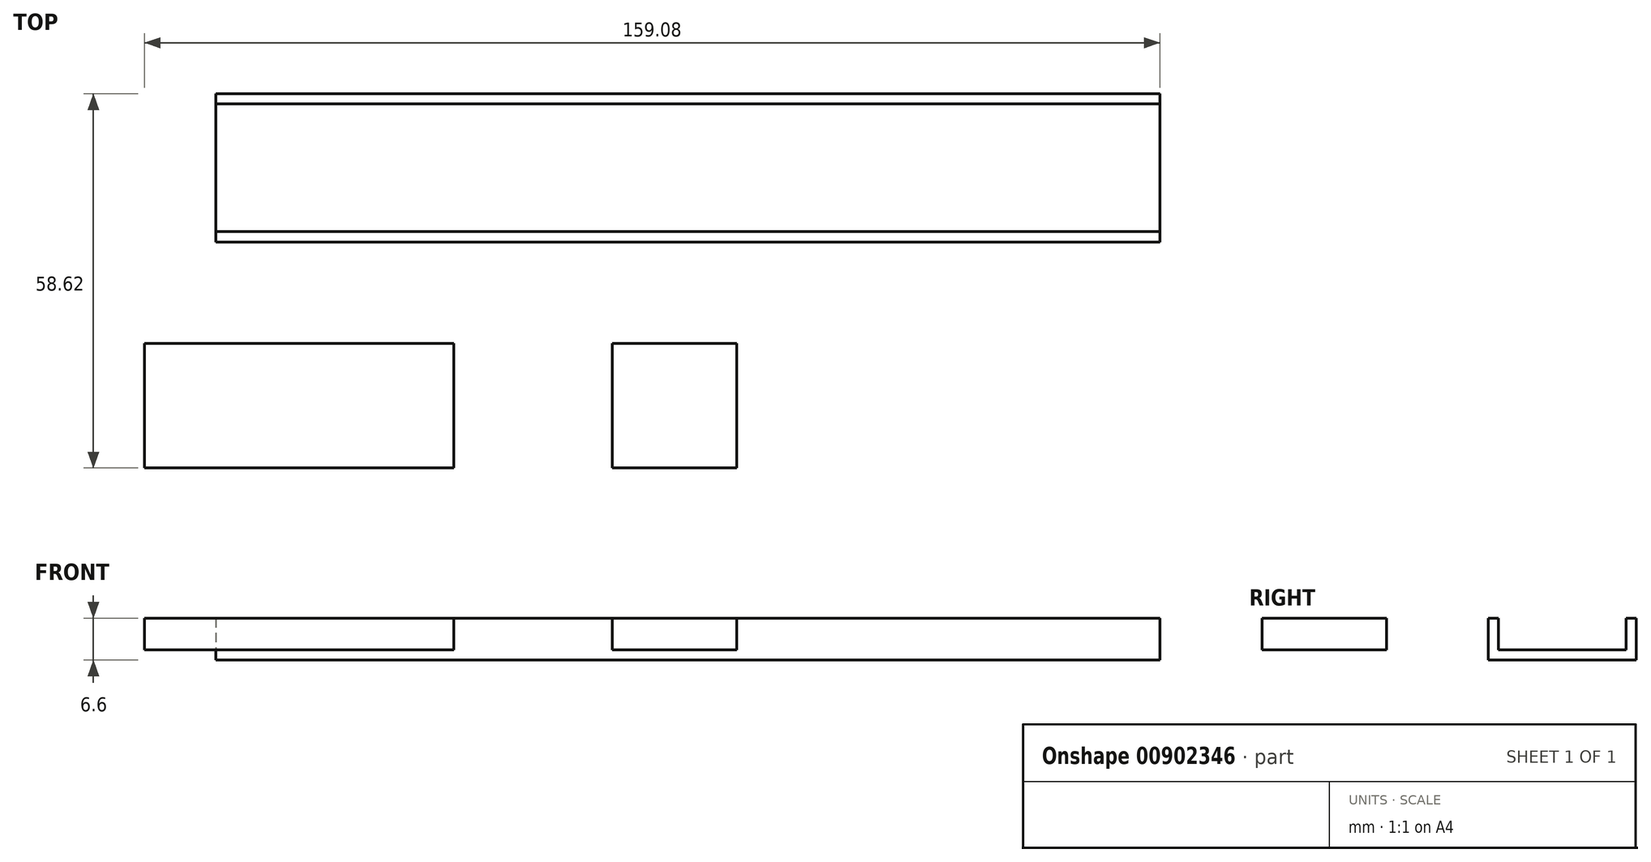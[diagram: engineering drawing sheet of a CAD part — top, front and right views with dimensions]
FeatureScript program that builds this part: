
annotation { "Feature Type Name" : "Feature", "Feature Type Description" : "" }
export const myFeature = defineFeature(function(context is Context, id is Id, definition is map)
    precondition{}
    {
        {
            var Q0;
            Q0=qCreatedBy(makeId("Top.planeOp"),FACE);
            var sketch = newSketch(context, id + "F0", { "sketchPlane" : qUnion([Q0])});
            skLineSegment(sketch, "E0.bottom", {"start": v(0, 0) * mm, "end": v(19.5, 0) * mm});
            skLineSegment(sketch, "E0.top", {"start": v(0, -19.5) * mm, "end": v(19.5, -19.5) * mm});
            skLineSegment(sketch, "E0.left", {"start": v(0, 0) * mm, "end": v(0, -19.5) * mm});
            skLineSegment(sketch, "E0.right", {"start": v(19.5, 0) * mm, "end": v(19.5, -19.5) * mm});
            skLineSegment(sketch, "E1.bottom", {"start": v(-24.79, 0) * mm, "end": v(-73.26, 0) * mm});
            skLineSegment(sketch, "E1.top", {"start": v(-24.79, -19.5) * mm, "end": v(-73.26, -19.5) * mm});
            skLineSegment(sketch, "E1.left", {"start": v(-24.79, 0) * mm, "end": v(-24.79, -19.5) * mm});
            skLineSegment(sketch, "E1.right", {"start": v(-73.26, 0) * mm, "end": v(-73.26, -19.5) * mm});
            skSolve(sketch);
        }
        {
            var Q0;
            Q0 = qSketchRegion(id + "F0", true);
            extrude(context, id + "F1", {"entities" : qUnion([Q0]), "depth" : 5 * mm, "offsetDistance" : 25 * mm});
        }
        {
            var Q0;
            Q0=qCreatedBy(makeId("Top.planeOp"),FACE);
            var sketch = newSketch(context, id + "F2", { "sketchPlane" : qUnion([Q0])});
            skLineSegment(sketch, "E2.bottom", {"start": v(-62.1, 37.52) * mm, "end": v(85.82, 37.52) * mm});
            skLineSegment(sketch, "E2.top", {"start": v(-62.1, 17.52) * mm, "end": v(85.82, 17.52) * mm});
            skLineSegment(sketch, "E2.left", {"start": v(-62.1, 37.52) * mm, "end": v(-62.1, 17.52) * mm});
            skLineSegment(sketch, "E2.right", {"start": v(85.82, 37.52) * mm, "end": v(85.82, 17.52) * mm});
            skSolve(sketch);
        }
        {
            var Q0;
            Q0 = qSketchRegion(id + "F2", true);
            extrude(context, id + "F3", {"entities" : qUnion([Q0]), "depth" : 5 * mm, "offsetDistance" : 25 * mm});
        }
        {
            var Q0;
            Q0=makeQuery(id+"F3.opExtrude","CAP_FACE",FACE,{"disambiguationData":[OSD([sQuery(id+"F2.wireOp",EDGE,"E2.bottom"),sQuery(id+"F2.wireOp",EDGE,"E2.top"),sQuery(id+"F2.wireOp",EDGE,"E2.left"),sQuery(id+"F2.wireOp",EDGE,"E2.right")])],"isStart":false});
            var Q1;
            Q1=makeQuery(id+"F3.opExtrude","SWEPT_FACE",FACE,{"disambiguationData":[OSD([sQuery(id+"F2.wireOp",EDGE,"E2.left")])]});
            var Q2;
            Q2=makeQuery(id+"F3.opExtrude","SWEPT_FACE",FACE,{"disambiguationData":[OSD([sQuery(id+"F2.wireOp",EDGE,"E2.right")])]});
            shell(context, id + "F4", {"entities" : qUnion([Q0, Q1, Q2]), "thickness" : 1.6 * mm, "oppositeDirection" : true});
        }
    });
